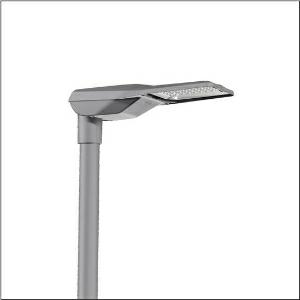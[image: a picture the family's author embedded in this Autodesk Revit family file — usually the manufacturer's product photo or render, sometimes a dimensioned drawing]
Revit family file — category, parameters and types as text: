
# Revit family: streetlight_sl_21_iq_mini___pl52_5xe2h41g08hb_e5d0
name_source: partatom
category: Lighting Fixtures
units: mm (PartAtom-declared; Revit-internal decimal feet)

## family parameters
Cut with Voids When Loaded = No
Host = Face
Light Source = No
Part Type = Normal
Room Calculation Point = No
Round Connector Dimension = Use Diameter
Shared = No

## types (1)
- --- (1 x LED, 9690 lm, 70.9 W, 4000K)
    Apparent Load = 71 VA
    CIE Flux Codes = 27 59 98 100 100
    Color Rendering = 70
    Color Temperature = 4000K
    Default Elevation = 1800 mm
    Description = Streetlight SL 21 iQ mini, mast luminaire, primary light control with lens, of PMMA, primary optical cover: cover, of toughened safety glass, transparent, light distribution: PL52, light emission: direct distribution, primary light characteristic: asymmetric, installation type: post-top, side-entry, LED, High Power LED, rated luminous flux: 9.690lm, luminous efficacy: 137lm/W, light colour: 740, colour temperature: 4000K, control gear: iQ Street-Remote, control: Street-Remote, Auto-Match, Temp-Guard, Lumen-Switch, Night-Set, Smart-Wire, Light-Fading, Desk-Remote (wireless, voltage-free reading and setting of iQ features in the workshop via application-optimized NFC function/RFID function), optimised constant luminous flux control (CLO 2.0), pre-setting: linear dimming characteristic, mains connection: 220..240V, AC, 50/60Hz, start of lifetime: 71W, end of service life: 75W, reduction: 31W, luminaire housing, of diecast aluminium, powder-coated, Siteco® metallic grey (DB 702S), corrosivity category C5 mid according to DIN EN ISO 12944, please order mast flange separately, inclination adjustable: 0°, 5°, 10°, 15°, sealing non-destructively replaceable, multi-level sealing system, length: 628mm, width: 235mm, height: 110mm, mast flange for spigot size: 42mm (side-entry): 5XC10008XM4, 60/48mm (side-entry/post-top): 5XC10108XM2, 76/60mm (side-entry/post-top): 5XC10108XM1, mounting height: 4..8m, protection rating (complete): IP66, insulation class (complete): insulation class II (safety insulation), certification: CE, ENEC, ENEC+, VDE, impact resistance: IK10, permissible operating ambient temperature for outdoor applications: -40..+50°C, standard-compliant lighting for roads and squares, packaging unit: 1 piece

Light Distribution: PL52
    Height = 110 mm
    Lamp = 1 x LED
    Lamp Light Flux = 9690 lm
    Lamp Power = 70.9 W
    Lamp count = 1
    Length = 625 mm
    Luminous efficacy = 137 lm/W
    Manufacturer = Siteco
    ModVariant = No
    Model = 5XE2H41G08HB
    Number of Poles = 1
    OnlyDefault = Yes
    Power Factor = 1
    Product Name = Streetlight SL 21 iQ mini | PL52
    Product group = mast luminaire | pylon top
    ProductGroupID = 6100
    Protection Class = Protection class II
    Protection Degree = IP 66
    RLX_Detail_Level = 1
    RLX_Emergency_Light_Flux = 0 lm
    RLX_Emergency_Type = 0
    RLX_Emergency_Type_DB = No
    RlxData = <blob elided: 35925 chars, md5=b4a6dc60>
    Socket = socket
    Standby Power = 0 W
    System Light Flux = 9690 lm
    System Power = 71 W
    Type Comments = factory setting: luminous flux: 100 % | dim-lin: 254 | 711 mA
    Type Image = l_1003519.jpg
    URL = http://relux.com
    VarID = @adj_179819
    Voltage = 0 V
    Weight = 0.00 kg
    Width = 234 mm

## geometry (parser evidence)
native form markers: Blend x4, Sweep x10
no freeform markers — native parametric forms only
